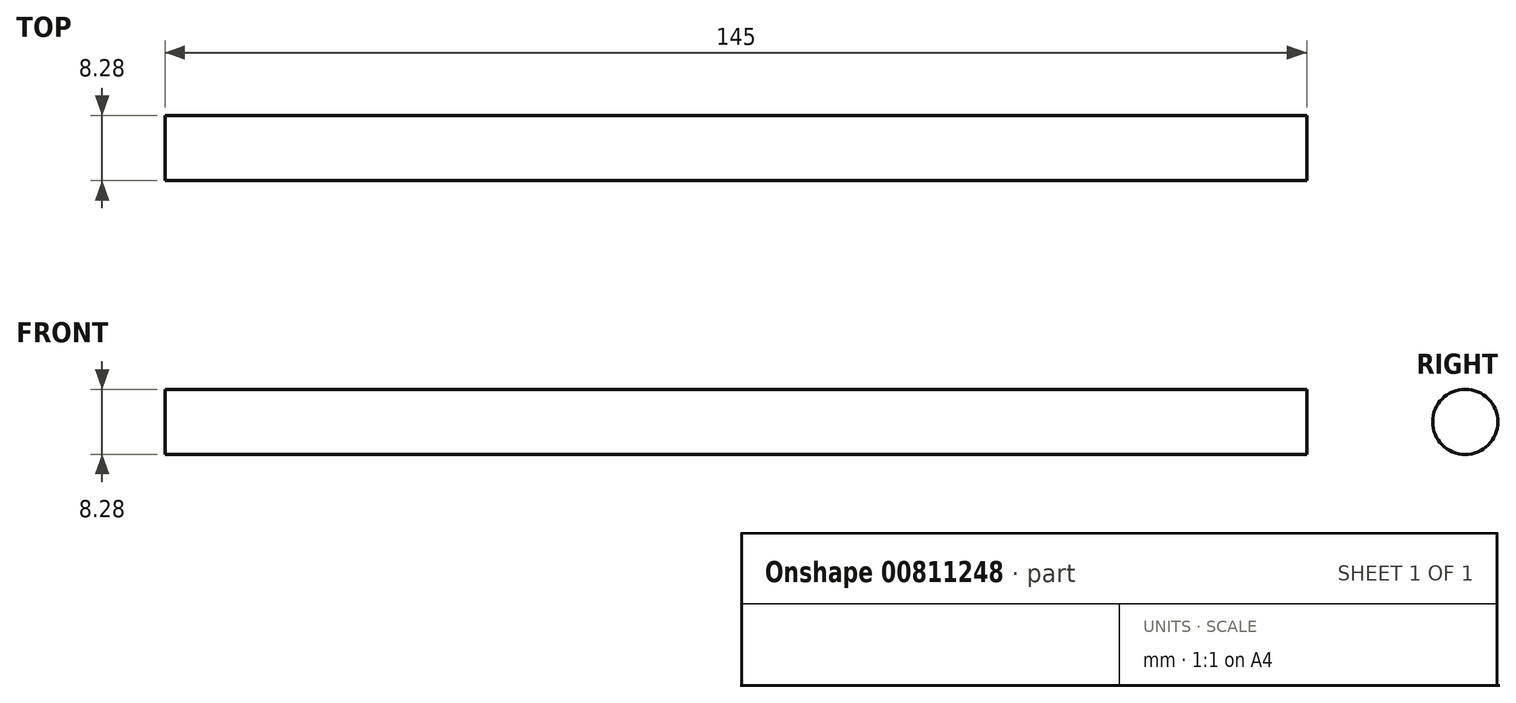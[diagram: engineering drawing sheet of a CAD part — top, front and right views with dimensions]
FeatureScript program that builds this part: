
annotation { "Feature Type Name" : "Feature", "Feature Type Description" : "" }
export const myFeature = defineFeature(function(context is Context, id is Id, definition is map)
    precondition{}
    {
        {
            var Q0;
            Q0=qCreatedBy(makeId("Right.planeOp"),FACE);
            var sketch = newSketch(context, id + "F0", { "sketchPlane" : qUnion([Q0])});
            skCircle(sketch, "E0", {"center": v(16.72, 5.9) * mm, "radius": 4.14 * mm});
            skSolve(sketch);
        }
        {
            var Q0;
            Q0 = qSketchRegion(id + "F0", true);
            extrude(context, id + "F1", {"entities" : qUnion([Q0]), "depth" : 145 * mm, "offsetDistance" : 25 * mm});
        }
    });
